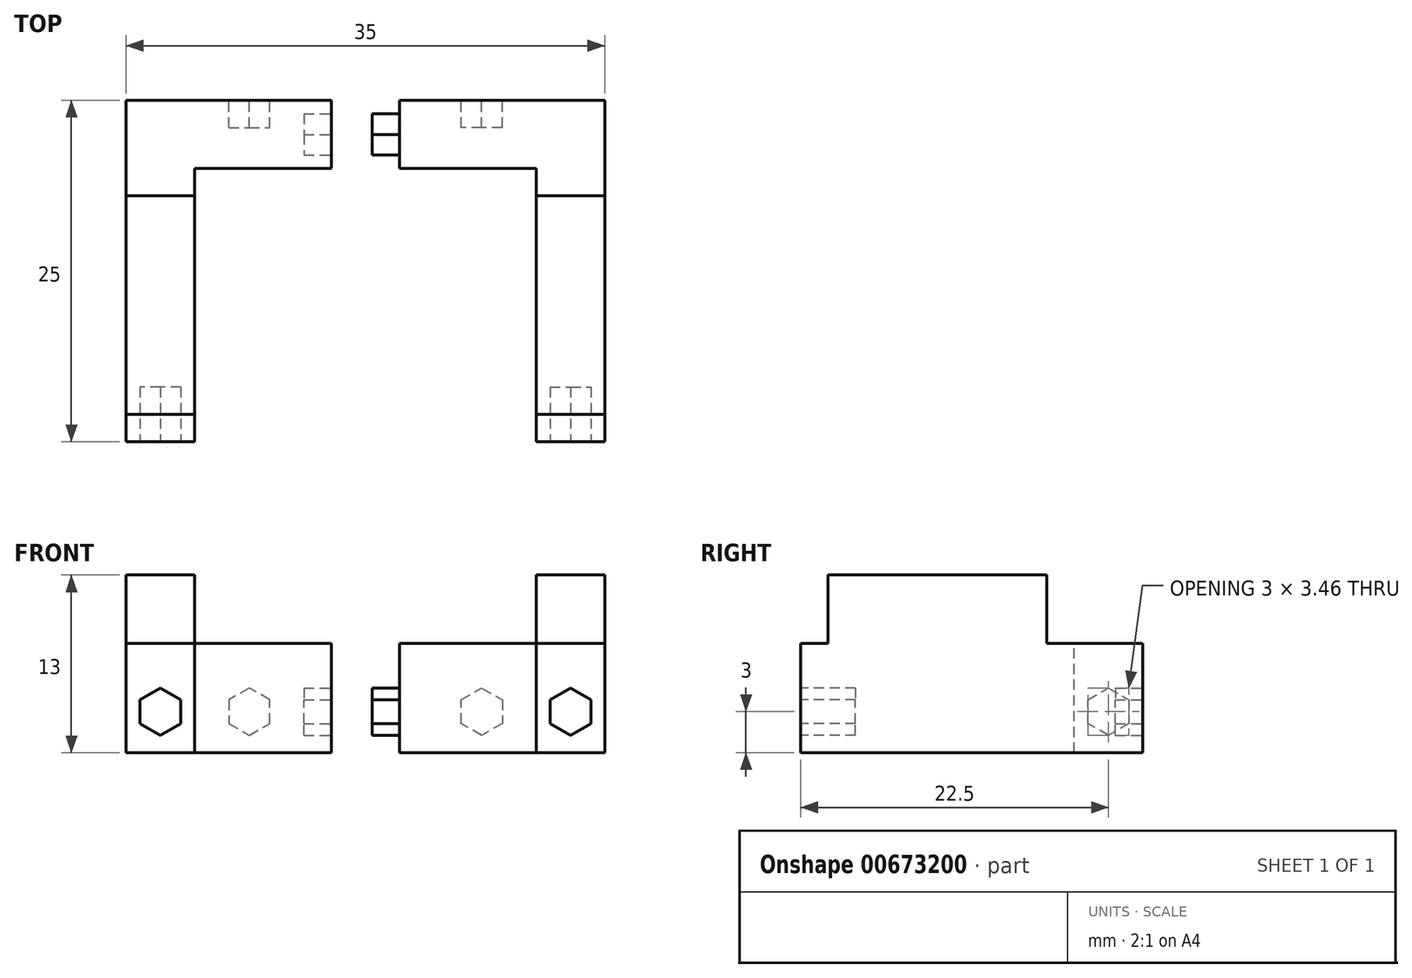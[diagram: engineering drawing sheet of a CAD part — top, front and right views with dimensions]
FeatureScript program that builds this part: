
annotation { "Feature Type Name" : "Feature", "Feature Type Description" : "" }
export const myFeature = defineFeature(function(context is Context, id is Id, definition is map)
    precondition{}
    {
        {
            var Q0;
            Q0=qCreatedBy(makeId("Right.planeOp"),FACE);
            var sketch = newSketch(context, id + "F0", { "sketchPlane" : qUnion([Q0])});
            skLineSegment(sketch, "E0.bottom", {"start": v(0, 0) * mm, "end": v(25, 0) * mm});
            skLineSegment(sketch, "E0.top", {"start": v(0, 8) * mm, "end": v(25, 8) * mm});
            skLineSegment(sketch, "E0.left", {"start": v(0, 0) * mm, "end": v(0, 8) * mm});
            skLineSegment(sketch, "E0.right", {"start": v(25, 0) * mm, "end": v(25, 8) * mm});
            skLineSegment(sketch, "E1", {"start": v(25, 0) * mm, "end": v(20, 0) * mm, "construction": true});
            skLineSegment(sketch, "E2", {"start": v(20, 0) * mm, "end": v(20, 8) * mm});
            skSolve(sketch);
        }
        {
            var Q0;
            Q0=qSketchRegion(id+"F0",true);
            extrude(context, id + "F1", {"entities" : qUnion([Q0]), "oppositeDirection" : true, "depth" : 5 * mm});
        }
        {
            var Q0;
            Q0=makeQuery(id+"F1.opExtrude","SWEPT_FACE",FACE,{"disambiguationData":[OSD([sQuery(id+"F0.wireOp",EDGE,"E0.left")])]});
            var sketch = newSketch(context, id + "F2", { "sketchPlane" : qUnion([Q0])});
            skLineSegment(sketch, "E3.bottom", {"start": v(0, 0) * mm, "end": v(-5, 0) * mm, "construction": true});
            skLineSegment(sketch, "E3.top", {"start": v(0, 6) * mm, "end": v(-5, 6) * mm, "construction": true});
            skLineSegment(sketch, "E3.left", {"start": v(-5, 0) * mm, "end": v(-5, 6) * mm, "construction": true});
            skLineSegment(sketch, "E3.right", {"start": v(0, 0) * mm, "end": v(0, 6) * mm, "construction": true});
            skCircle(sketch, "E4.cCircle", {"center": v(-2.5, 3) * mm, "radius": 1.5 * mm, "construction": true});
            skPoint(sketch, "E4.cCircle.centerSnap0", {"position": v(-5, 3) * mm});
            skPoint(sketch, "E4.cCircle.centerSnap1", {"position": v(-2.5, 6) * mm});
            skLineSegment(sketch, "E4.0", {"start": v(-4, 2.13) * mm, "end": v(-4, 3.87) * mm});
            skLineSegment(sketch, "E4.1", {"start": v(-4, 3.87) * mm, "end": v(-2.5, 4.73) * mm});
            skLineSegment(sketch, "E4.2", {"start": v(-2.5, 4.73) * mm, "end": v(-1, 3.87) * mm});
            skLineSegment(sketch, "E4.3", {"start": v(-1, 3.87) * mm, "end": v(-1, 2.13) * mm});
            skLineSegment(sketch, "E4.4", {"start": v(-1, 2.13) * mm, "end": v(-2.5, 1.27) * mm});
            skLineSegment(sketch, "E4.5", {"start": v(-2.5, 1.27) * mm, "end": v(-4, 2.13) * mm});
            skPoint(sketch, "E4.0.midPoint", {"position": v(-4, 3) * mm});
            skSolve(sketch);
        }
        {
            var Q0;
            Q0=qSketchRegion(id+"F2",true);
            extrude(context, id + "F3", {"entities" : qUnion([Q0]), "operationType" : NewBodyOperationType.REMOVE, "oppositeDirection" : true, "depth" : 4 * mm});
        }
        {
            var Q0;
            {var subQ0=sQuery(id+"F0.wireOp",EDGE,"E0.right");Q0=makeQuery(id+"F0.imprint","IMPRINT",FACE,{"disambiguationData":[TD([[makeQuery(id+"F0.imprint","IMPRINT",EDGE,{"derivedFrom":subQ0}),1.0]])]});}
            extrude(context, id + "F4", {"entities" : qUnion([Q0]), "operationType" : NewBodyOperationType.ADD, "depth" : 10 * mm});
        }
        {
            var Q0;
            Q0=makeQuery(id+"F4.opExtrude","CAP_FACE",FACE,{"disambiguationData":[OSD([sQuery(id+"F0.wireOp",EDGE,"E0.bottom"),sQuery(id+"F0.wireOp",EDGE,"E0.top"),sQuery(id+"F0.wireOp",EDGE,"E0.right"),sQuery(id+"F0.wireOp",EDGE,"E2")])],"isStart":false});
            var sketch = newSketch(context, id + "F5", { "sketchPlane" : qUnion([Q0])});
            skLineSegment(sketch, "E5.bottom", {"start": v(25, 0) * mm, "end": v(20, 0) * mm, "construction": true});
            skLineSegment(sketch, "E5.top", {"start": v(25, 6) * mm, "end": v(20, 6) * mm, "construction": true});
            skLineSegment(sketch, "E5.left", {"start": v(25, 0) * mm, "end": v(25, 6) * mm, "construction": true});
            skLineSegment(sketch, "E5.right", {"start": v(20, 0) * mm, "end": v(20, 6) * mm, "construction": true});
            skPoint(sketch, "E6.cCircle.centerSnap0", {"position": v(25, 3) * mm});
            skPoint(sketch, "E6.cCircle.centerSnap1", {"position": v(22.5, 6) * mm});
            skLineSegment(sketch, "E6.0", {"start": v(21, 2.13) * mm, "end": v(21, 3.87) * mm});
            skLineSegment(sketch, "E6.1", {"start": v(21, 3.87) * mm, "end": v(22.5, 4.73) * mm});
            skLineSegment(sketch, "E6.2", {"start": v(22.5, 4.73) * mm, "end": v(24, 3.87) * mm});
            skLineSegment(sketch, "E6.3", {"start": v(24, 3.87) * mm, "end": v(24, 2.13) * mm});
            skLineSegment(sketch, "E6.4", {"start": v(24, 2.13) * mm, "end": v(22.5, 1.27) * mm});
            skLineSegment(sketch, "E6.5", {"start": v(22.5, 1.27) * mm, "end": v(21, 2.13) * mm});
            skPoint(sketch, "E6.0.midPoint", {"position": v(21, 3) * mm});
            skSolve(sketch);
        }
        {
            var Q0;
            Q0=makeQuery(id+"F5.imprint","IMPRINT",FACE,{"disambiguationData":[TD([[makeQuery(id+"F5.imprint","IMPRINT",EDGE,{"derivedFrom":sQuery(id+"F5.wireOp",EDGE,"E6.0")}),-1.0]])]});
            extrude(context, id + "F6", {"entities" : qUnion([Q0]), "operationType" : NewBodyOperationType.REMOVE, "oppositeDirection" : true, "depth" : 2 * mm});
        }
        {
            var Q0;
            {var subQ0=sQuery(id+"F0.wireOp",EDGE,"E0.right");Q0=makeQuery(id+"F4.boolean.opBoolean","MERGE",FACE,{"derivedFrom":[makeQuery(id+"F1.opExtrude","SWEPT_FACE",FACE,{"disambiguationData":[OSD([subQ0])]}),makeQuery(id+"F4.opExtrude","SWEPT_FACE",FACE,{"disambiguationData":[OSD([subQ0])]})]});}
            var sketch = newSketch(context, id + "F7", { "sketchPlane" : qUnion([Q0])});
            skLineSegment(sketch, "E7.bottom", {"start": v(-6.5, 0) * mm, "end": v(-1.5, 0) * mm, "construction": true});
            skLineSegment(sketch, "E7.top", {"start": v(-6.5, 6) * mm, "end": v(-1.5, 6) * mm, "construction": true});
            skLineSegment(sketch, "E7.left", {"start": v(-6.5, 0) * mm, "end": v(-6.5, 6) * mm, "construction": true});
            skLineSegment(sketch, "E7.right", {"start": v(-1.5, 0) * mm, "end": v(-1.5, 6) * mm, "construction": true});
            skCircle(sketch, "E8.cCircle", {"center": v(-4, 3) * mm, "radius": 1.5 * mm, "construction": true});
            skPoint(sketch, "E8.cCircle.centerSnap0", {"position": v(-4, 6) * mm});
            skPoint(sketch, "E8.cCircle.centerSnap1", {"position": v(-1.5, 3) * mm});
            skPoint(sketch, "E8.cCircle.perimeterSnap0", {"position": v(-1.5, 3) * mm});
            skLineSegment(sketch, "E8.0", {"start": v(-5.5, 2.13) * mm, "end": v(-5.5, 3.87) * mm});
            skLineSegment(sketch, "E8.1", {"start": v(-5.5, 3.87) * mm, "end": v(-4, 4.73) * mm});
            skLineSegment(sketch, "E8.2", {"start": v(-4, 4.73) * mm, "end": v(-2.5, 3.87) * mm});
            skLineSegment(sketch, "E8.3", {"start": v(-2.5, 3.87) * mm, "end": v(-2.5, 2.13) * mm});
            skLineSegment(sketch, "E8.4", {"start": v(-2.5, 2.13) * mm, "end": v(-4, 1.27) * mm});
            skLineSegment(sketch, "E8.5", {"start": v(-4, 1.27) * mm, "end": v(-5.5, 2.13) * mm});
            skPoint(sketch, "E8.0.midPoint", {"position": v(-5.5, 3) * mm});
            skPoint(sketch, "E8.0.midPoint.positionSnap0", {"position": v(-1.5, 3) * mm});
            skSolve(sketch);
        }
        {
            var Q0;
            Q0=qSketchRegion(id+"F7",true);
            extrude(context, id + "F8", {"entities" : qUnion([Q0]), "operationType" : NewBodyOperationType.REMOVE, "oppositeDirection" : true, "depth" : 2 * mm});
        }
        {
            var Q0;
            Q0=qCreatedBy(makeId("Right.planeOp"),FACE);
            cPlane(context, id + "F9", {"entities" : qUnion([Q0]), "cplaneType" : CPlaneType.OFFSET, "offset" : 12.5 * mm, "width" : 150 * mm, "height" : 150 * mm});
        }
        {
            var Q0;
            Q0=makeQuery(id+"F1.opExtrude","SWEPT_BODY",BODY,{"disambiguationData":[OSD([sQuery(id+"F0.wireOp",EDGE,"E0.bottom"),sQuery(id+"F0.wireOp",EDGE,"E0.top"),sQuery(id+"F0.wireOp",EDGE,"E0.left"),sQuery(id+"F0.wireOp",EDGE,"E0.right")])]});
            var Q1;
            Q1=qCreatedBy(id+"F9.planeOp",FACE);
            mirror(context, id + "F10", {"entities" : qUnion([Q0]), "mirrorPlane" : qUnion([Q1])});
        }
        {
            var Q0;
            Q0=makeQuery(id+"F10.opPattern","COPY",FACE,{"derivedFrom":makeQuery(id+"F6.boolean.opBoolean","COPY",FACE,{"derivedFrom":makeQuery(id+"F6.opExtrude","CAP_FACE",FACE,{"disambiguationData":[OSD([sQuery(id+"F5.wireOp",EDGE,"E6.0"),sQuery(id+"F5.wireOp",EDGE,"E6.1"),sQuery(id+"F5.wireOp",EDGE,"E6.2"),sQuery(id+"F5.wireOp",EDGE,"E6.3"),sQuery(id+"F5.wireOp",EDGE,"E6.4"),sQuery(id+"F5.wireOp",EDGE,"E6.5")])],"isStart":false})}),"instanceName":"1"});
            extrude(context, id + "F11", {"entities" : qUnion([Q0]), "operationType" : NewBodyOperationType.ADD, "depth" : 4 * mm});
        }
        {
            var Q0;
            {var subQ0=sQuery(id+"F0.wireOp",EDGE,"E0.top");Q0=makeQuery(id+"F4.boolean.opBoolean","MERGE",FACE,{"derivedFrom":[makeQuery(id+"F1.opExtrude","SWEPT_FACE",FACE,{"disambiguationData":[OSD([subQ0])]}),makeQuery(id+"F4.opExtrude","SWEPT_FACE",FACE,{"disambiguationData":[OSD([subQ0])]})]});}
            var sketch = newSketch(context, id + "F12", { "sketchPlane" : qUnion([Q0])});
            skLineSegment(sketch, "E9.bottom", {"start": v(0, 20) * mm, "end": v(-5, 20) * mm});
            skLineSegment(sketch, "E9.left", {"start": v(0, 20) * mm, "end": v(0, 2) * mm});
            skLineSegment(sketch, "E9.right", {"start": v(-5, 20) * mm, "end": v(-5, 2) * mm});
            skLineSegment(sketch, "E10", {"start": v(0.83, 0) * mm, "end": v(0.83, 2) * mm, "construction": true});
            skLineSegment(sketch, "E11", {"start": v(0, 2) * mm, "end": v(-5, 2) * mm});
            skPoint(sketch, "E9.top.start.orphan", {"position": v(0, 0) * mm});
            skSolve(sketch);
        }
        {
            var Q0;
            Q0=qSketchRegion(id+"F12",true);
            extrude(context, id + "F13", {"entities" : qUnion([Q0]), "operationType" : NewBodyOperationType.ADD, "depth" : 5 * mm});
        }
        {
            var Q0;
            {var subQ0=sQuery(id+"F0.wireOp",EDGE,"E0.top");Q0=makeQuery(id+"F10.opPattern","COPY",FACE,{"derivedFrom":makeQuery(id+"F4.boolean.opBoolean","MERGE",FACE,{"derivedFrom":[makeQuery(id+"F1.opExtrude","SWEPT_FACE",FACE,{"disambiguationData":[OSD([subQ0])]}),makeQuery(id+"F4.opExtrude","SWEPT_FACE",FACE,{"disambiguationData":[OSD([subQ0])]})]}),"instanceName":"1"});}
            var sketch = newSketch(context, id + "F14", { "sketchPlane" : qUnion([Q0])});
            skLineSegment(sketch, "E12.bottom", {"start": v(25, 20) * mm, "end": v(30, 20) * mm});
            skLineSegment(sketch, "E12.left", {"start": v(25, 20) * mm, "end": v(25, 2) * mm});
            skLineSegment(sketch, "E12.right", {"start": v(30, 20) * mm, "end": v(30, 2) * mm});
            skLineSegment(sketch, "E13", {"start": v(31.57, 0) * mm, "end": v(31.57, 2) * mm, "construction": true});
            skLineSegment(sketch, "E14", {"start": v(30, 2) * mm, "end": v(25, 2) * mm});
            skSolve(sketch);
        }
        {
            var Q0;
            Q0=qSketchRegion(id+"F14",true);
            extrude(context, id + "F15", {"entities" : qUnion([Q0]), "operationType" : NewBodyOperationType.ADD, "depth" : 5 * mm});
        }
        {
            var Q0;
            Q0=makeQuery(id+"F13.opExtrude","SWEPT_FACE",FACE,{"disambiguationData":[OSD([sQuery(id+"F12.wireOp",EDGE,"E9.bottom")])]});
            extrude(context, id + "F16", {"entities" : qUnion([Q0]), "operationType" : NewBodyOperationType.REMOVE, "oppositeDirection" : true, "depth" : 2 * mm});
        }
        {
            var Q0;
            Q0=makeQuery(id+"F15.opExtrude","SWEPT_FACE",FACE,{"disambiguationData":[OSD([sQuery(id+"F14.wireOp",EDGE,"E12.bottom")])]});
            extrude(context, id + "F17", {"entities" : qUnion([Q0]), "operationType" : NewBodyOperationType.REMOVE, "oppositeDirection" : true, "depth" : 2 * mm});
        }
    });
